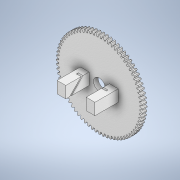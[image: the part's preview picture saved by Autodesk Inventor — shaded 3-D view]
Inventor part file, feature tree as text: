
AUTODESK INVENTOR PART (.ipt)
format: ipt  version: 2022.2 (Build 262287010, 287A)  size: 551,936 bytes
history: native  units: mm (DEFAULTED — no unit token found)
features: sketch x7, extrude x5, plane x3, other x3, mirror x1
ambient origin geometry x8: Origin, YZ Plane, XZ Plane, XY Plane, X Axis, Y Axis, Z Axis, Center Point
bodies: Solid1 (feature_tree)
feature tree (19):
  extrude  "Extrusion1"  Depth=8.0mm TaperAngle=0.0deg
  plane  "Work Plane2"
  plane  "Work Plane8"
  plane  "Work Plane9"
  other  "Engranaje recto"
  extrude  "Extrusión2"  Depth=10.0mm TaperAngle=0.0deg
  sketch  "Boceto4"  dims[d16=90.0mm d17=0.0mm d34=0.436332mm]
  extrude  "Extrusión9"  Depth=0.436332mm TaperAngle=0.0deg
  sketch  "Boceto18"  dims[d43=90.0mm d46=90.0mm]
  extrude  "Extrusión14"  TaperAngle=0.0deg  [1 undecoded]
  extrude  "Extrusión16"  Depth=90.0mm
  mirror  "Simetría3"
  sketch  "Sketch2"  dims[d0=148.0mm d1=8.0mm d2=0.0mm]
  other  "Srf1"
  sketch  "Boceto3"  dims[d3=144.0mm d4=10.0mm d5=0.0mm]
  sketch  "Boceto9"  dims[d39=0.0mm d41=0.0mm]
  sketch  "Boceto19"  dims[d47=0.0mm d48=0.0mm]
  sketch  "Boceto20"  dims[d49=20.0mm d50=0.0mm d51=0.0mm d54=25.0mm d58=15.0mm d59=20.0mm d87=1.5mm d93=5.0mm d94=1.0mm d95=0.0mm d96=40.0mm d97=25.0mm d113=55.0mm d114=80.0mm d115=70.0mm d116=5.0mm d117=40.0mm d119=360.0deg d123=40.0mm d124=0.0mm d125=20.0mm d126=15.0mm d127=25.0mm d128=15.0mm d129=25.0mm d134=30.5mm d135=10.5mm d136=3.1mm d137=3.1mm d138=8.0mm d139=0.0mm d84=0.5mm d85=0.872665mm d86=0.5mm d107=0.5mm d108=0.872665mm d109=0.5mm d110=0.872665mm]
  other  "Diámetro de separación"
note: 1 required parameter value undecoded (feature->parameter linkage not recoverable at this tier; creation-order binding heuristic only, values carry confidence <= 0.55)
